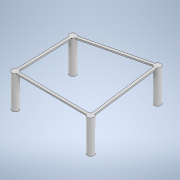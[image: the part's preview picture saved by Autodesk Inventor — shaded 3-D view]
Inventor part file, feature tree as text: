
AUTODESK INVENTOR PART (.ipt)
format: ipt  version: 2021 (Build 250183000, 183)  size: 4,097,024 bytes
history: native  units: mm
features: sketch x5, extrude x2, other x2, plane x1
ambient origin geometry x8: Origin, YZ Plane, XZ Plane, XY Plane, X Axis, Y Axis, Z Axis, Center Point
bodies: Volumenkörper1 (feature_tree)
feature tree (10):
  sketch  "Skizze1"  dims[d41=4.5mm d46=5.788582mm]
  extrude  "Extrusion1"  Depth=5.788582mm
  extrude  "Extrusion2"  Depth=7.698439mm
  sketch  "Skizze7"  dims[d73=291.757338mm]
  plane  "Arbeitsebene1"
  sketch  "Skizze5"  dims[d68=239.216569mm]
  other  "Spirale1"
  sketch  "Skizzenbasierte Anordnung1"  dims[d47=4.5mm d51=7.698439mm]
  other  "Bild2"
  sketch  "Skizze8"  dims[d74=4.5mm d75=4.5mm d92=4.509385mm d93=6.006555mm d94=302.019293mm d95=331.775478mm d97=341.309338mm d101=8.8mm d102=1.0mm d104=14.436981mm d141=1.0mm d165=90.0deg d168=1.0mm d170=1.0mm d172=1.0mm d173=0.4mm d174=3.54225mm d175=6.0mm d176=6.0mm d177=3.54225mm d178=6.0mm d179=3.54225mm d180=6.0mm d181=3.54225mm d185=2.4mm d187=2.4mm d191=2.4mm d192=2.4mm d193=1.2mm d194=0.0mm d195=30.0mm d196=0.0mm d214=60.0deg d215=4.3mm d216=0.7mm d217=3.54225mm d218=0.378875mm d219=0.075775mm d220=60.0deg d221=4.3mm d222=0.7mm d223=3.54225mm d224=0.6062mm d226=90.0deg d229=0.7mm d230=10.0mm d231=100.0mm d232=0.0mm d233=90.0deg d234=90.0deg d235=0.0mm d236=0.0mm d237=55.922254mm d244=60.0deg d245=6.3mm d246=1.0mm d247=5.2175mm d248=0.866mm]
